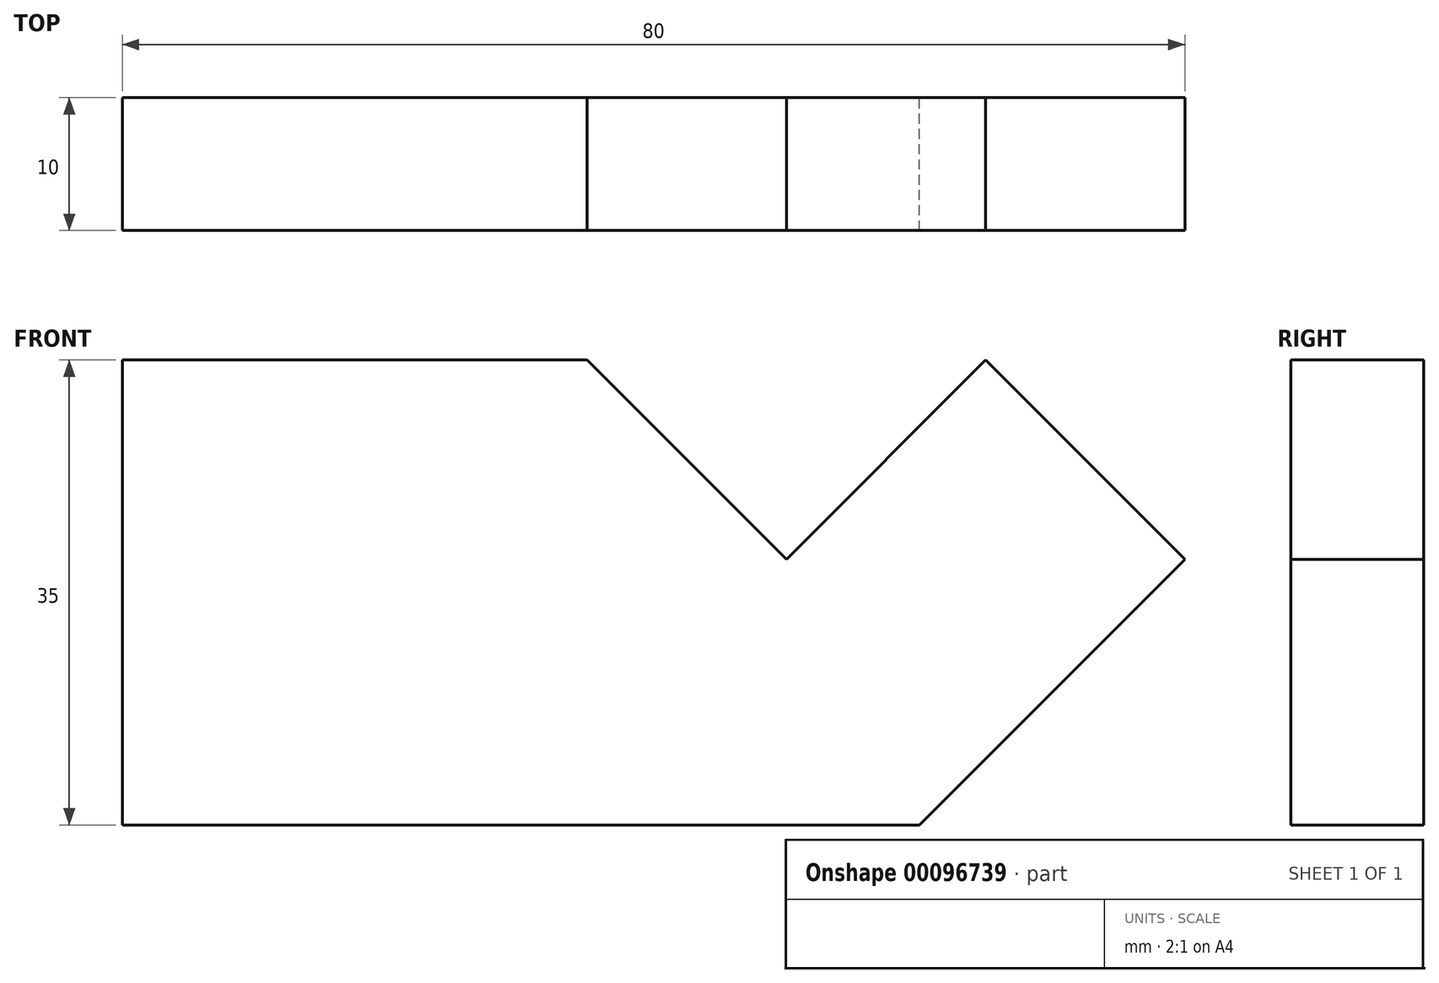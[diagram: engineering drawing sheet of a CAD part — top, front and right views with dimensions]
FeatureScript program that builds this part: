
annotation { "Feature Type Name" : "Feature", "Feature Type Description" : "" }
export const myFeature = defineFeature(function(context is Context, id is Id, definition is map)
    precondition{}
    {
        {
            var Q0;
            Q0=qCreatedBy(makeId("Front.planeOp"),FACE);
            var sketch = newSketch(context, id + "F0", { "sketchPlane" : qUnion([Q0])});
            skLineSegment(sketch, "E0", {"start": v(0, 0) * mm, "end": v(0, 35) * mm});
            skLineSegment(sketch, "E1", {"start": v(0, 35) * mm, "end": v(35, 35) * mm});
            skLineSegment(sketch, "E2", {"start": v(50, 20) * mm, "end": v(65, 35) * mm});
            skLineSegment(sketch, "E3", {"start": v(0, 0) * mm, "end": v(60, 0) * mm});
            skLineSegment(sketch, "E4", {"start": v(60, 0) * mm, "end": v(80, 20) * mm});
            skLineSegment(sketch, "E5", {"start": v(65, 35) * mm, "end": v(80, 20) * mm});
            skLineSegment(sketch, "E6", {"start": v(35, 35) * mm, "end": v(50, 20) * mm});
            skSolve(sketch);
        }
        {
            var Q0;
            Q0 = qSketchRegion(id + "F0", true);
            extrude(context, id + "F1", {"entities" : qUnion([Q0]), "depth" : 10 * mm});
        }
    });
